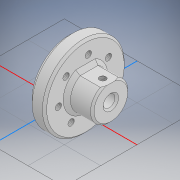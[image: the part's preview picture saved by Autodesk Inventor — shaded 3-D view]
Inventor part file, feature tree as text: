
AUTODESK INVENTOR PART (.ipt)
format: ipt  version: 2022 (Build 260153000, 153)  size: 361,472 bytes
history: native  units: mm
features: thread x8, other x7, extrude x6, sketch x6, chamfer x4, projected_geometry x1
ambient origin geometry x8: Origin, YZ Plane, XZ Plane, XY Plane, X Axis, Y Axis, Z Axis, Center Point
bodies: Body1 (feature_tree)
feature tree (32):
  extrude  "Выдавливание1"  Depth=14.0mm TaperAngle=0.0deg
  extrude  "Выдавливание3"  Depth=6.5mm
  other  "РабПлоскость1"
  extrude  "Выдавливание7"  Depth=10.0mm TaperAngle=0.0deg
  extrude  "Выдавливание8"  TaperAngle=0.0deg  [1 undecoded]
  extrude  "Выдавливание9"  Depth=9.0mm
  chamfer  "Фаска2"  Distance=1.0mm
  chamfer  "Фаска3"  Distance=10.0mm
  chamfer  "Фаска4"  Distance=1.0mm Angle=45.0deg
  extrude  "Выдавливание10"  Depth=1.0mm TaperAngle=45.0deg
  other  "Непосредственное редактирование2"
  chamfer  "Фаска5"  Distance=2.0mm Angle=45.0deg
  other  "Непосредственное редактирование3"
  thread  "Резьба9"
  thread  "Резьба10"
  thread  "Резьба11"
  thread  "Резьба12"
  thread  "Резьба13"
  thread  "Резьба14"
  thread  "Резьба15"
  thread  "Резьба16"
  other  "Твердое тело5"
  sketch  "Эскиз1"
  sketch  "Эскиз3"
  sketch  "Эскиз7"
  sketch  "Эскиз8"
  projected_geometry  "Спроецированная петля2"
  sketch  "Эскиз9"
  sketch  "Эскиз10"
  other  "Solid1:4"
  other  "Размер1"
  other  "Размер2"
note: 1 required parameter value undecoded (feature->parameter linkage not recoverable at this tier; creation-order binding heuristic only, values carry confidence <= 0.55)
